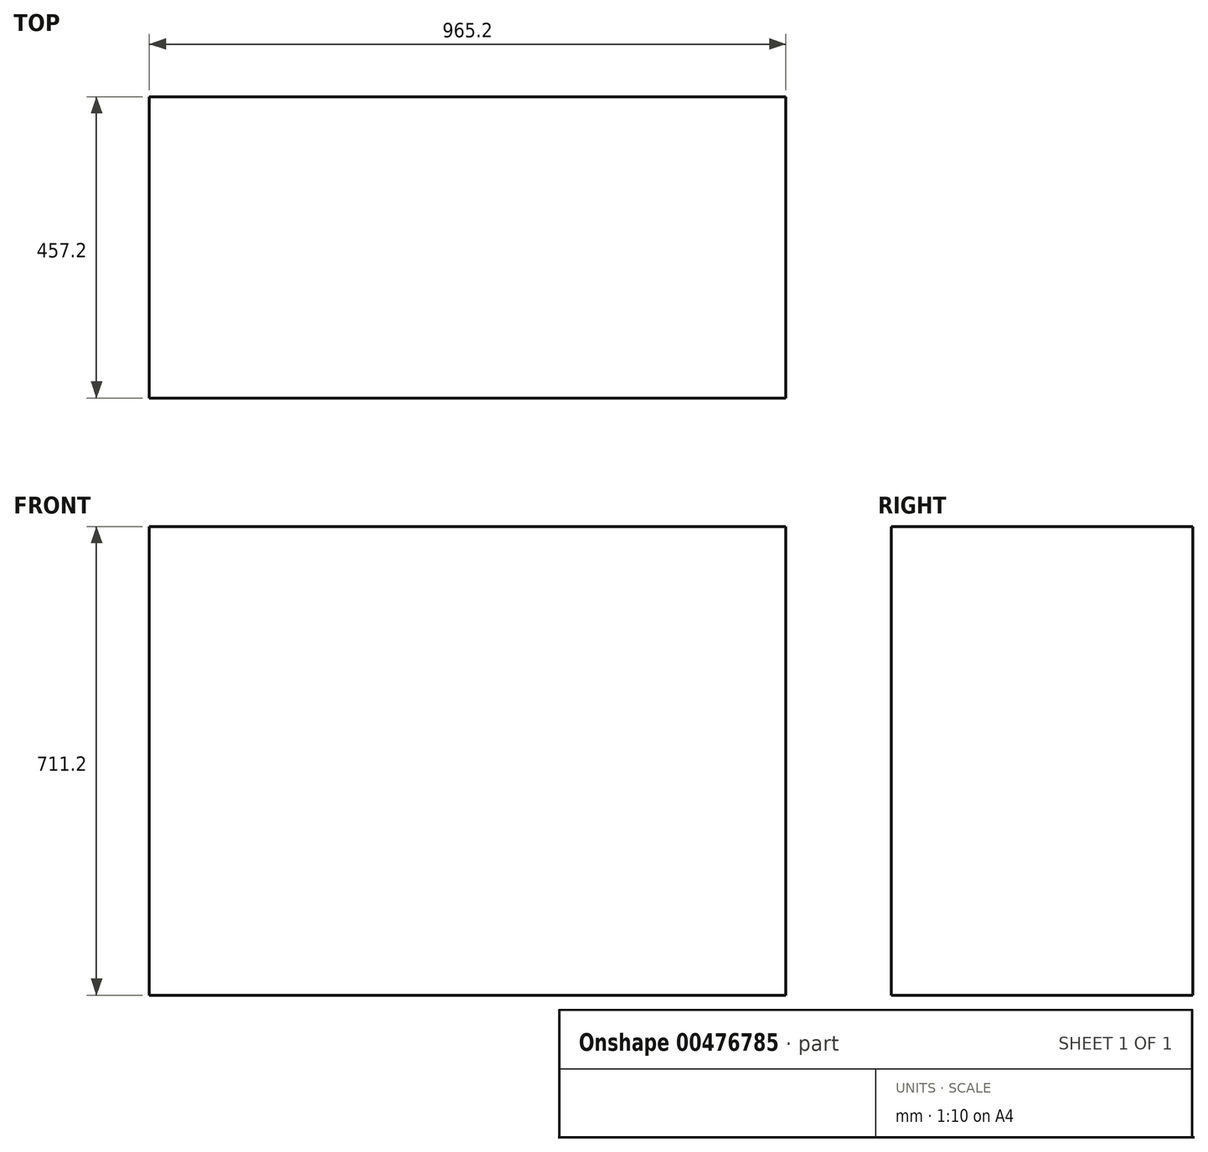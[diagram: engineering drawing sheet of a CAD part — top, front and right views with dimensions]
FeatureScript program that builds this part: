
annotation { "Feature Type Name" : "Feature", "Feature Type Description" : "" }
export const myFeature = defineFeature(function(context is Context, id is Id, definition is map)
    precondition{}
    {
        {
            var Q0;
            Q0=qCreatedBy(makeId("Top.planeOp"),FACE);
            var sketch = newSketch(context, id + "F0", { "sketchPlane" : qUnion([Q0])});
            skLineSegment(sketch, "E0.bottom", {"start": v(0, 0) * mm, "end": v(965.2, 0) * mm});
            skLineSegment(sketch, "E0.top", {"start": v(0, 457.2) * mm, "end": v(965.2, 457.2) * mm});
            skLineSegment(sketch, "E0.left", {"start": v(0, 0) * mm, "end": v(0, 457.2) * mm});
            skLineSegment(sketch, "E0.right", {"start": v(965.2, 0) * mm, "end": v(965.2, 457.2) * mm});
            skSolve(sketch);
        }
        {
            var Q0;
            Q0=qSketchRegion(id+"F0",true);
            extrude(context, id + "F1", {"entities" : qUnion([Q0]), "depth" : 711.2 * mm});
        }
    });
